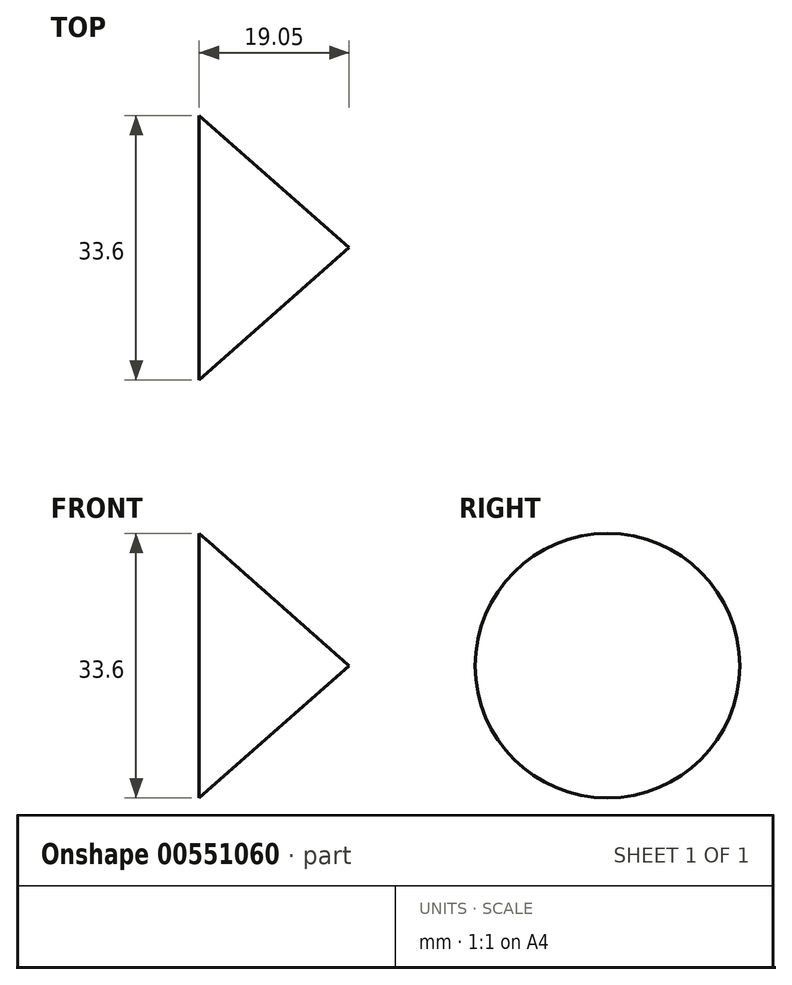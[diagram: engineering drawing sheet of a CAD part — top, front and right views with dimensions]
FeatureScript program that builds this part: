
annotation { "Feature Type Name" : "Feature", "Feature Type Description" : "" }
export const myFeature = defineFeature(function(context is Context, id is Id, definition is map)
    precondition{}
    {
        {
            var Q0;
            Q0=qCreatedBy(makeId("Front.planeOp"),FACE);
            var sketch = newSketch(context, id + "F0", { "sketchPlane" : qUnion([Q0])});
            skLineSegment(sketch, "E0", {"start": v(0, 0) * mm, "end": v(19.05, 0) * mm});
            skLineSegment(sketch, "E1", {"start": v(19.05, 0) * mm, "end": v(0, -16.8) * mm});
            skLineSegment(sketch, "E2", {"start": v(0, -16.8) * mm, "end": v(0, 0) * mm});
            skSolve(sketch);
        }
        {
            var Q0;
            Q0=makeQuery(id+"F0.imprint","IMPRINT",FACE,{"disambiguationData":[TD([[makeQuery(id+"F0.imprint","IMPRINT",EDGE,{"derivedFrom":sQuery(id+"F0.wireOp",EDGE,"E0")}),-1.0]])]});
            var Q1;
            Q1=sQuery(id+"F0.wireOp",EDGE,"E0");
            revolve(context, id + "F1", {"entities" : qUnion([Q0]), "axis" : qUnion([Q1]), "revolveType" : RevolveType.FULL});
        }
    });
